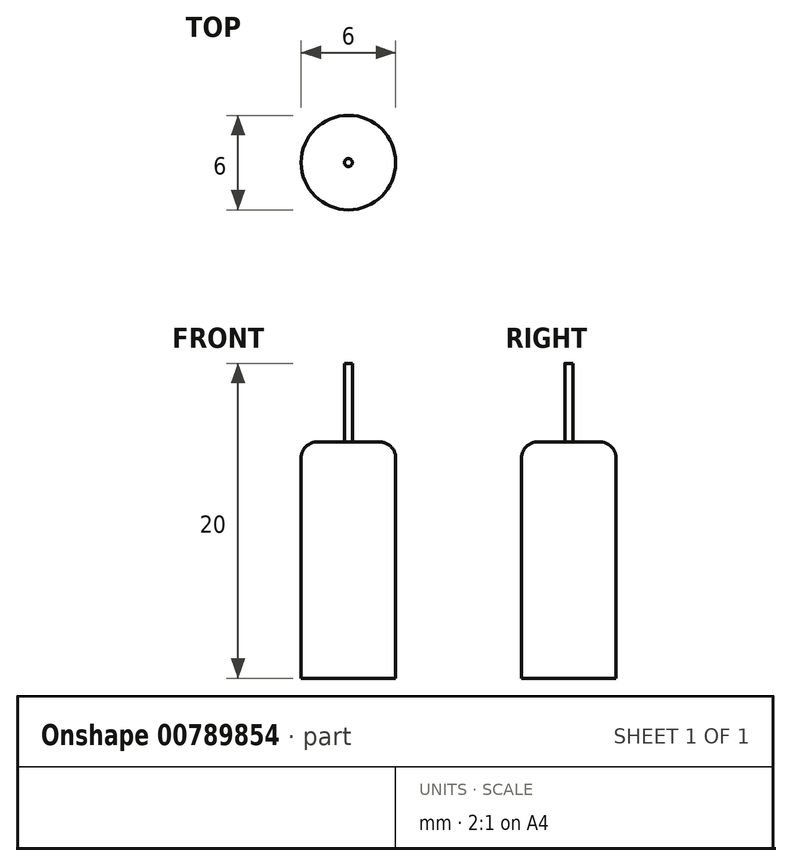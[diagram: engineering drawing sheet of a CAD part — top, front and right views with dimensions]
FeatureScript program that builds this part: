
annotation { "Feature Type Name" : "Feature", "Feature Type Description" : "" }
export const myFeature = defineFeature(function(context is Context, id is Id, definition is map)
    precondition{}
    {
        {
            var Q0;
            Q0=qCreatedBy(makeId("Top.planeOp"),FACE);
            var sketch = newSketch(context, id + "F0", { "sketchPlane" : qUnion([Q0])});
            skCircle(sketch, "E0", {"center": v(0, 0) * mm, "radius": 3 * mm});
            skSolve(sketch);
        }
        {
            var Q0;
            Q0=makeQuery(id+"F0.imprint","IMPRINT",FACE,{"disambiguationData":[TD([[makeQuery(id+"F0.imprint","IMPRINT",EDGE,{"derivedFrom":sQuery(id+"F0.wireOp",EDGE,"E0")}),1.0]])]});
            extrude(context, id + "F1", {"entities" : qUnion([Q0]), "depth" : 15 * mm, "offsetDistance" : 25 * mm});
        }
        {
            var Q0;
            Q0=makeQuery(id+"F1.opExtrude","CAP_FACE",FACE,{"disambiguationData":[OSD([sQuery(id+"F0.wireOp",EDGE,"E0")])],"isStart":false});
            var sketch = newSketch(context, id + "F2", { "sketchPlane" : qUnion([Q0])});
            skCircle(sketch, "E1", {"center": v(0, 0) * mm, "radius": 0.25 * mm});
            skSolve(sketch);
        }
        {
            var Q0;
            Q0=makeQuery(id+"F2.imprint","IMPRINT",FACE,{"disambiguationData":[TD([[makeQuery(id+"F2.imprint","IMPRINT",EDGE,{"derivedFrom":sQuery(id+"F2.wireOp",EDGE,"E1")}),1.0]])]});
            extrude(context, id + "F3", {"entities" : qUnion([Q0]), "operationType" : NewBodyOperationType.ADD, "depth" : 5 * mm, "offsetDistance" : 25 * mm});
        }
        {
            var Q0;
            Q0=makeQuery(id+"F1.opExtrude","CAP_EDGE",EDGE,{"disambiguationData":[OSD([sQuery(id+"F0.wireOp",EDGE,"E0")])],"isStart":false});
            fillet(context, id + "F4", {"entities" : qUnion([Q0]), "radius" : 1 * mm, "tangentPropagation" : true, "allowEdgeOverflow" : false});
        }
    });
